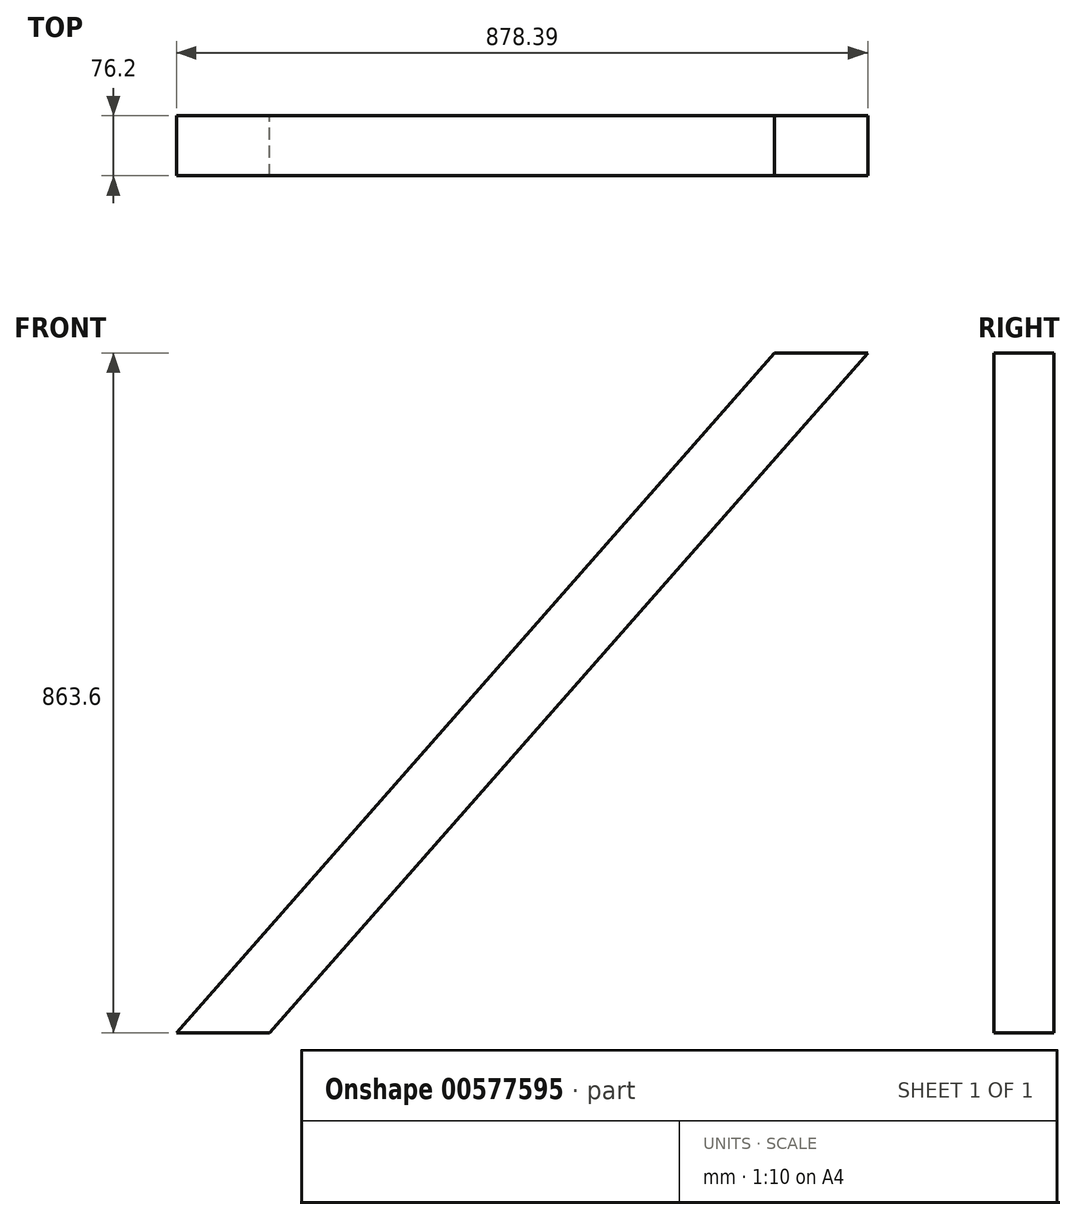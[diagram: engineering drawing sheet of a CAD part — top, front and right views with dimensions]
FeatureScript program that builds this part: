
annotation { "Feature Type Name" : "Feature", "Feature Type Description" : "" }
export const myFeature = defineFeature(function(context is Context, id is Id, definition is map)
    precondition{}
    {
        {
            var Q0;
            Q0=qCreatedBy(makeId("Front.planeOp"),FACE);
            var sketch = newSketch(context, id + "F0", { "sketchPlane" : qUnion([Q0])});
            skLineSegment(sketch, "E0", {"start": v(0, 0) * mm, "end": v(0, 2247.9) * mm});
            skLineSegment(sketch, "E1", {"start": v(0, 2247.9) * mm, "end": v(1460.5, 2247.9) * mm});
            skLineSegment(sketch, "E2", {"start": v(1460.5, 2247.9) * mm, "end": v(1460.5, 863.6) * mm});
            skLineSegment(sketch, "E3", {"start": v(901.7, 0) * mm, "end": v(0, 0) * mm});
            skLineSegment(sketch, "E4", {"start": v(1661.67, 863.6) * mm, "end": v(1460.5, 863.6) * mm});
            skLineSegment(sketch, "E5", {"start": v(901.7, 0) * mm, "end": v(1661.67, 863.6) * mm});
            skSolve(sketch);
        }
        {
            var Q0;
            Q0=makeQuery(id+"F0.imprint","IMPRINT",FACE,{"disambiguationData":[TD([[makeQuery(id+"F0.imprint","IMPRINT",EDGE,{"derivedFrom":sQuery(id+"F0.wireOp",EDGE,"E0")}),-1.0]])]});
            var sketch = newSketch(context, id + "F1", { "sketchPlane" : qUnion([Q0])});
            skLineSegment(sketch, "E6", {"start": v(1661.67, 863.6) * mm, "end": v(901.7, 0) * mm});
            skLineSegment(sketch, "E7", {"start": v(901.7, 0) * mm, "end": v(783.28, 0) * mm});
            skLineSegment(sketch, "E8", {"start": v(783.28, 0) * mm, "end": v(1543.25, 863.6) * mm});
            skLineSegment(sketch, "E9", {"start": v(1543.25, 863.6) * mm, "end": v(1661.67, 863.6) * mm});
            skSolve(sketch);
        }
        {
            var Q0;
            Q0 = qSketchRegion(id + "F1", true);
            extrude(context, id + "F2", {"entities" : qUnion([Q0]), "depth" : 76.2 * mm, "offsetDistance" : 25.4 * mm});
        }
    });
